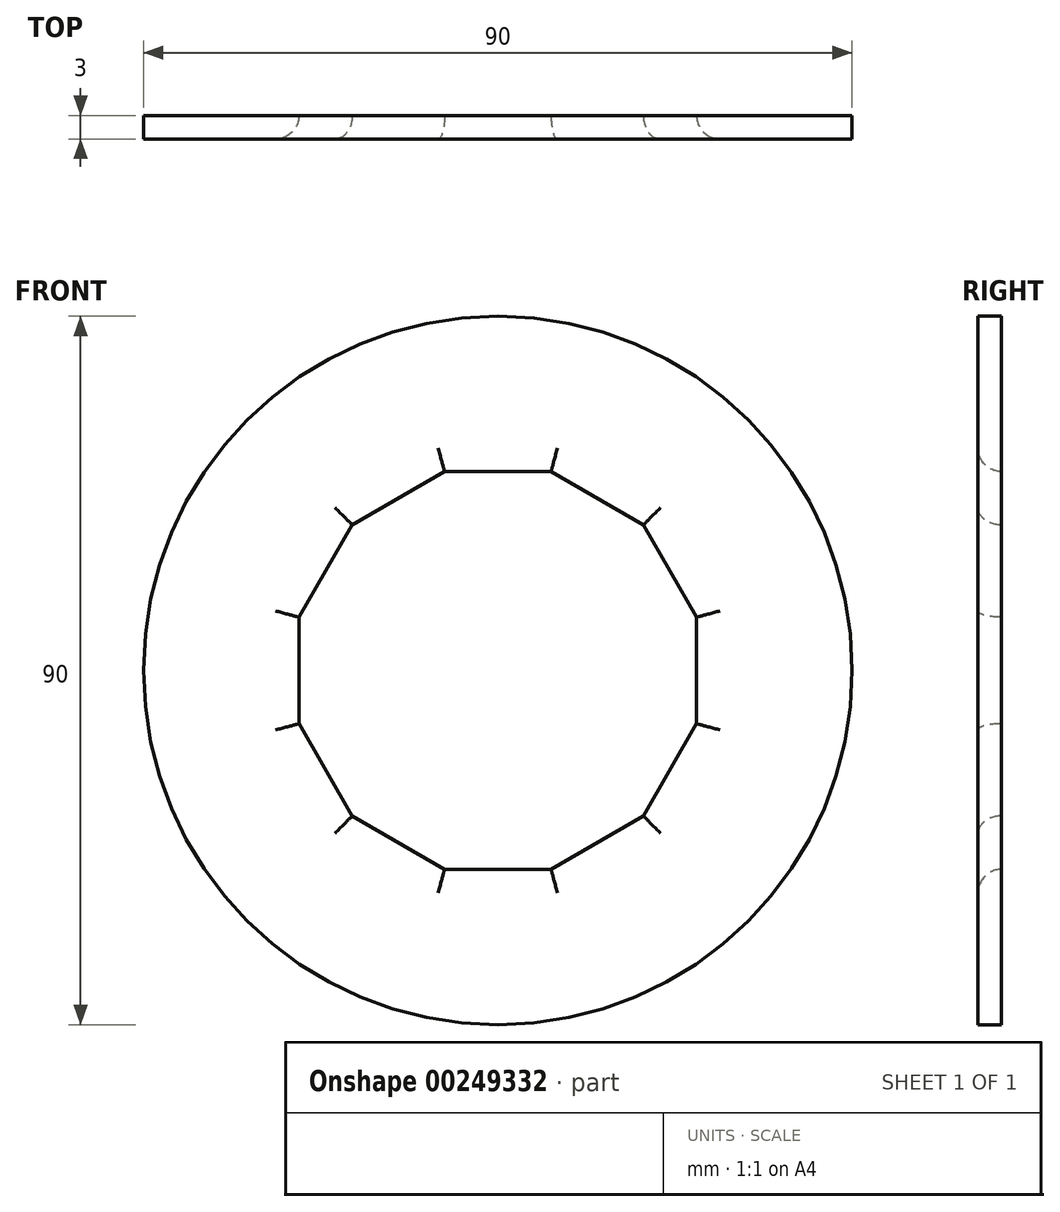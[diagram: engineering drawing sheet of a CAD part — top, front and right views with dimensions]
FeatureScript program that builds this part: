
annotation { "Feature Type Name" : "Feature", "Feature Type Description" : "" }
export const myFeature = defineFeature(function(context is Context, id is Id, definition is map)
    precondition{}
    {
        {
            var Q0;
            Q0=qCreatedBy(makeId("Front.planeOp"),FACE);
            var sketch = newSketch(context, id + "F0", { "sketchPlane" : qUnion([Q0])});
            skCircle(sketch, "E0.cCircle", {"center": v(0, 0) * mm, "radius": 25.25 * mm, "construction": true});
            skLineSegment(sketch, "E0.0", {"start": v(-6.77, 25.25) * mm, "end": v(6.77, 25.25) * mm});
            skLineSegment(sketch, "E0.1", {"start": v(6.77, 25.25) * mm, "end": v(18.48, 18.48) * mm});
            skLineSegment(sketch, "E0.2", {"start": v(18.48, 18.48) * mm, "end": v(25.25, 6.77) * mm});
            skLineSegment(sketch, "E0.3", {"start": v(25.25, 6.77) * mm, "end": v(25.25, -6.77) * mm});
            skLineSegment(sketch, "E0.4", {"start": v(25.25, -6.77) * mm, "end": v(18.48, -18.48) * mm});
            skLineSegment(sketch, "E0.5", {"start": v(18.48, -18.48) * mm, "end": v(6.77, -25.25) * mm});
            skLineSegment(sketch, "E0.6", {"start": v(6.77, -25.25) * mm, "end": v(-6.77, -25.25) * mm});
            skLineSegment(sketch, "E0.7", {"start": v(-6.77, -25.25) * mm, "end": v(-18.48, -18.48) * mm});
            skLineSegment(sketch, "E0.8", {"start": v(-18.48, -18.48) * mm, "end": v(-25.25, -6.77) * mm});
            skLineSegment(sketch, "E0.9", {"start": v(-25.25, -6.77) * mm, "end": v(-25.25, 6.77) * mm});
            skLineSegment(sketch, "E0.10", {"start": v(-25.25, 6.77) * mm, "end": v(-18.48, 18.48) * mm});
            skLineSegment(sketch, "E0.11", {"start": v(-18.48, 18.48) * mm, "end": v(-6.77, 25.25) * mm});
            skPoint(sketch, "E0.0.midPoint", {"position": v(0, 25.25) * mm});
            skCircle(sketch, "E1", {"center": v(0, 0) * mm, "radius": 45 * mm});
            skSolve(sketch);
        }
        {
            var Q0;
            Q0=makeQuery(id+"F0.imprint","IMPRINT",FACE,{"disambiguationData":[TD([[makeQuery(id+"F0.imprint","IMPRINT",EDGE,{"derivedFrom":sQuery(id+"F0.wireOp",EDGE,"E0.0")}),1.0]])]});
            extrude(context, id + "F1", {"entities" : qUnion([Q0]), "depth" : 3 * mm});
        }
        {
            var Q0;
            Q0=makeQuery(id+"F1.opExtrude","CAP_EDGE",EDGE,{"disambiguationData":[OSD([sQuery(id+"F0.wireOp",EDGE,"E0.11")])],"isStart":false});
            var Q1;
            Q1=makeQuery(id+"F1.opExtrude","CAP_EDGE",EDGE,{"disambiguationData":[OSD([sQuery(id+"F0.wireOp",EDGE,"E0.10")])],"isStart":false});
            var Q2;
            Q2=makeQuery(id+"F1.opExtrude","CAP_EDGE",EDGE,{"disambiguationData":[OSD([sQuery(id+"F0.wireOp",EDGE,"E0.9")])],"isStart":false});
            var Q3;
            Q3=makeQuery(id+"F1.opExtrude","CAP_EDGE",EDGE,{"disambiguationData":[OSD([sQuery(id+"F0.wireOp",EDGE,"E0.8")])],"isStart":false});
            var Q4;
            Q4=makeQuery(id+"F1.opExtrude","CAP_EDGE",EDGE,{"disambiguationData":[OSD([sQuery(id+"F0.wireOp",EDGE,"E0.7")])],"isStart":false});
            var Q5;
            Q5=makeQuery(id+"F1.opExtrude","CAP_EDGE",EDGE,{"disambiguationData":[OSD([sQuery(id+"F0.wireOp",EDGE,"E0.6")])],"isStart":false});
            var Q6;
            Q6=makeQuery(id+"F1.opExtrude","CAP_EDGE",EDGE,{"disambiguationData":[OSD([sQuery(id+"F0.wireOp",EDGE,"E0.5")])],"isStart":false});
            var Q7;
            Q7=makeQuery(id+"F1.opExtrude","CAP_EDGE",EDGE,{"disambiguationData":[OSD([sQuery(id+"F0.wireOp",EDGE,"E0.4")])],"isStart":false});
            var Q8;
            Q8=makeQuery(id+"F1.opExtrude","CAP_EDGE",EDGE,{"disambiguationData":[OSD([sQuery(id+"F0.wireOp",EDGE,"E0.3")])],"isStart":false});
            var Q9;
            Q9=makeQuery(id+"F1.opExtrude","CAP_EDGE",EDGE,{"disambiguationData":[OSD([sQuery(id+"F0.wireOp",EDGE,"E0.2")])],"isStart":false});
            var Q10;
            Q10=makeQuery(id+"F1.opExtrude","CAP_EDGE",EDGE,{"disambiguationData":[OSD([sQuery(id+"F0.wireOp",EDGE,"E0.1")])],"isStart":false});
            var Q11;
            Q11=makeQuery(id+"F1.opExtrude","CAP_EDGE",EDGE,{"disambiguationData":[OSD([sQuery(id+"F0.wireOp",EDGE,"E0.0")])],"isStart":false});
            fillet(context, id + "F2", {"entities" : qUnion([Q0, Q1, Q2, Q3, Q4, Q5, Q6, Q7, Q8, Q9, Q10, Q11]), "radius" : 3 * mm, "tangentPropagation" : true, "allowEdgeOverflow" : false});
        }
    });
